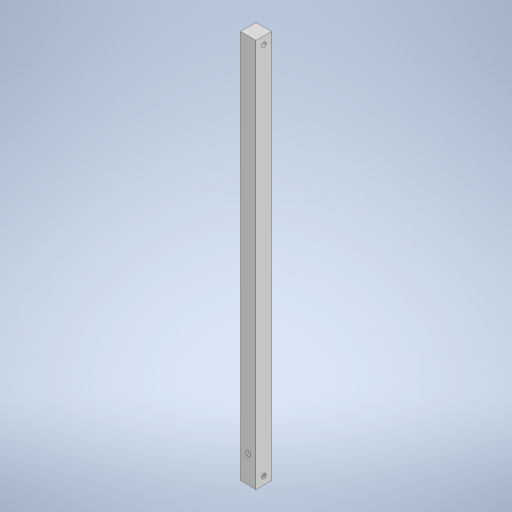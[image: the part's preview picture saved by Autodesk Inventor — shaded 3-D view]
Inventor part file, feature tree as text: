
AUTODESK INVENTOR PART (.ipt)
format: ipt  version: 2023 (Build 270158000, 158)  size: 247,296 bytes
history: native  units: mm
features: sketch x3, hole x2, other x1, extrude x1
ambient origin geometry x8: Origin, YZ Plane, XZ Plane, XY Plane, X Axis, Y Axis, Z Axis, Center Point
bodies: Body1 (feature_tree)
feature tree (7):
  other  "ソリッド1"
  extrude  "押し出し1"  Depth=10.0mm
  hole  "穴1"  [1 undecoded]
  hole  "穴2"  [1 undecoded]
  sketch  "スケッチ1"
  sketch  "スケッチ2"
  sketch  "スケッチ3"
note: 2 required parameter values undecoded (feature->parameter linkage not recoverable at this tier; creation-order binding heuristic only, values carry confidence <= 0.55)
